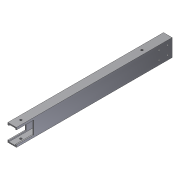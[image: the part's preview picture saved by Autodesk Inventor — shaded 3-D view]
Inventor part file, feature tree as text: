
AUTODESK INVENTOR PART (.ipt)
format: ipt  version: 2012 (Build 160160000, 160)  size: 124,928 bytes
history: native  units: in
note: dims shown in document units (in); Inventor stores cm internally (conversion verified against a paired STEP export)
features: extrude x4, sketch x4, shell x1
ambient origin geometry x8: Origin, YZ Plane, XZ Plane, XY Plane, X Axis, Y Axis, Z Axis, Center Point
bodies: Solid1 (feature_tree)
feature tree (9):
  extrude  "Extrusion1"  Depth=2.0in
  shell  "Shell1"  Thickness=18.0in
  extrude  "Extrusion2"  Depth=26.0in TaperAngle=0.0deg
  extrude  "Extrusion3"  Depth=3.0in
  extrude  "Extrusion4"  Depth=0.5in
  sketch  "Sketch1"  dims[d0=1.0in d1=2.0in d2=18.0in d3=0.0in]
  sketch  "Sketch2"  dims[d4=0.125in d13=26.0in d14=0.0in]
  sketch  "Sketch3"  dims[d15=0.5in d16=3.0in]
  sketch  "Sketch4"  dims[d17=0.25in d18=0.5in d19=0.25in d20=1.0in d21=26.0in d22=0.0in d24=1.5in d26=0.25in d27=16.0in d28=2.0in d29=0.1875in d30=0.5in d31=1.0in d32=1.0in d33=0.5in d34=1.0in d35=0.0in]
